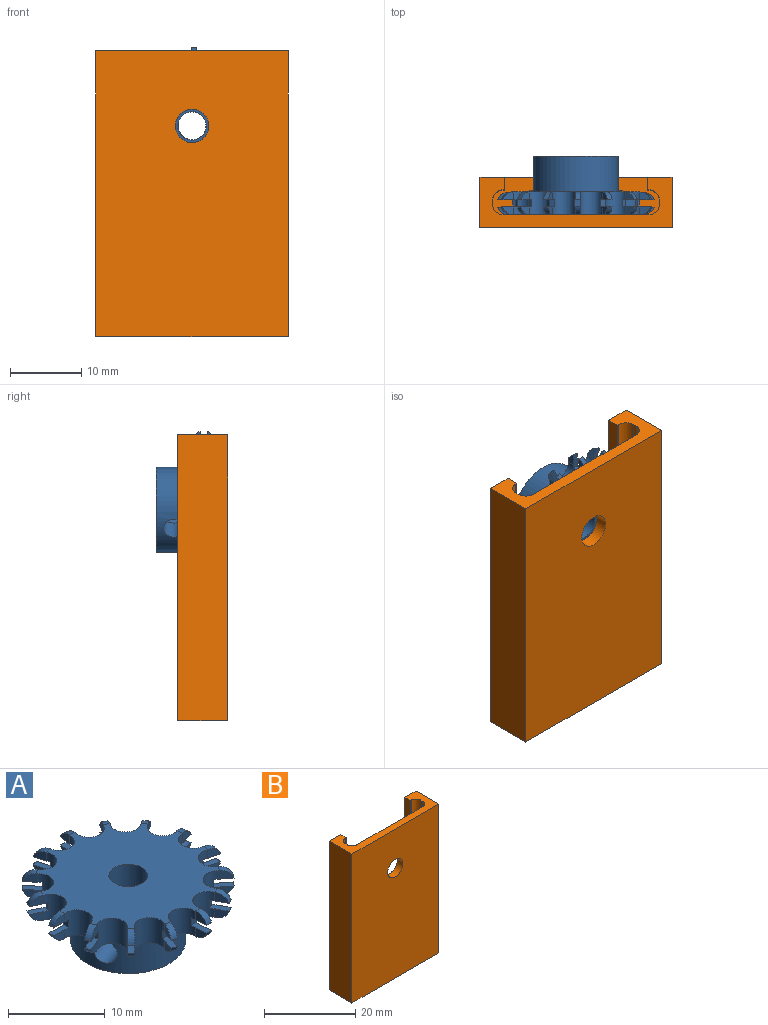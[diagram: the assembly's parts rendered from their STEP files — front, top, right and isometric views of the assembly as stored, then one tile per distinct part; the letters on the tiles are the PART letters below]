
ASSEMBLY  parts=2 mates=1
PART A: 186 faces, bbox 21.9x21.9x8.2 mm
  f0: plane 0.69x0.21mm, normal (-0.29,0.96,0), area 0mm2, adj f153,f183
  f1: plane 0.55x0.47mm, normal (-0.65,0.76,0), area 0mm2, adj f149,f181
  f2: plane 0.66x0.31mm, normal (-0.9,0.43,0), area 0mm2, adj f146,f179
  f3: plane 0.62x0.02mm, normal (-1,0.02,0), area 0mm2, adj f143,f177
  f4: plane 0.67x0.28mm, normal (-0.92,-0.39,0), area 0mm2, adj f140,f175
  f5: plane 0.53x0.5mm, normal (-0.69,-0.73,0), area 0mm2, adj f137,f173
  f6: plane 0.68x0.24mm, normal (-0.33,-0.94,0), area 0mm2, adj f134,f171
  f7: plane 0.72x0.06mm, normal (0.08,-1,0), area 0mm2, adj f131,f169
  f8: plane 0.64x0.35mm, normal (0.48,-0.88,0), area 0mm2, adj f128,f167
  f9: plane 0.58x0.44mm, normal (0.8,-0.61,0), area 0mm2, adj f125,f165
  f10: plane 0.71x0.17mm, normal (0.97,-0.23,0), area 0mm2, adj f122,f163
  f11: plane 0.71x0.13mm, normal (0.98,0.19,0), area 0mm2, adj f119,f161
  f12: plane 0.6x0.41mm, normal (0.82,0.57,0), area 0mm2, adj f116,f159
  f13: plane 0.62x0.38mm, normal (0.52,0.85,0), area 0mm2, adj f113,f157
  f14: plane 1.54x1.1mm, normal (0.96,0.29,0), area 1.3mm2, adj f84,f90,f154,f184
  f15: plane 1.57x1.13mm, normal (-0.96,-0.29,0), area 1.3mm2, adj f84,f91,f154,f184
  f16: plane 1.22x1.1mm, normal (0.76,0.65,0), area 1.3mm2, adj f84,f91,f150,f182
  f17: plane 1.25x1.13mm, normal (-0.76,-0.65,0), area 1.3mm2, adj f84,f92,f150,f182
  f18: plane 1.45x1.1mm, normal (0.43,0.9,0), area 1.3mm2, adj f84,f92,f147,f180
  f19: plane 1.48x1.13mm, normal (-0.43,-0.9,0), area 1.3mm2, adj f84,f93,f147,f180
  f20: plane 1.6x1.1mm, normal (0.02,1,0), area 1.3mm2, adj f84,f93,f144,f178
  f21: plane 1.63x1.13mm, normal (-0.02,-1,0), area 1.3mm2, adj f84,f94,f144,f178
  f22: plane 1.48x1.1mm, normal (-0.39,0.92,0), area 1.3mm2, adj f84,f94,f141,f176
  f23: plane 1.51x1.13mm, normal (0.39,-0.92,0), area 1.3mm2, adj f84,f95,f141,f176
  f24: plane 1.17x1.1mm, normal (-0.73,0.69,0), area 1.3mm2, adj f84,f95,f138,f174
  f25: plane 1.2x1.13mm, normal (0.73,-0.69,0), area 1.3mm2, adj f84,f96,f138,f174
  f26: plane 1.51x1.1mm, normal (-0.94,0.33,0), area 1.3mm2, adj f84,f96,f135,f172
  f27: plane 1.54x1.13mm, normal (0.94,-0.33,0), area 1.3mm2, adj f84,f97,f135,f172
  f28: plane 1.6x1.1mm, normal (-1,-0.08,0), area 1.3mm2, adj f84,f97,f132,f170
  f29: plane 1.63x1.13mm, normal (1,0.08,0), area 1.3mm2, adj f84,f98,f132,f170
  f30: plane 1.41x1.1mm, normal (-0.88,-0.48,0), area 1.3mm2, adj f84,f98,f129,f168
  f31: plane 1.44x1.13mm, normal (0.88,0.48,0), area 1.3mm2, adj f84,f99,f129,f168
  f32: plane 1.28x1.1mm, normal (-0.61,-0.8,0), area 1.3mm2, adj f84,f99,f126,f166
  f33: plane 1.31x1.13mm, normal (0.61,0.8,0), area 1.3mm2, adj f84,f100,f126,f166
  f34: plane 1.56x1.1mm, normal (-0.23,-0.97,0), area 1.3mm2, adj f84,f100,f123,f164
  f35: plane 1.59x1.13mm, normal (0.23,0.97,0), area 1.3mm2, adj f84,f101,f123,f164
  f36: plane 1.58x1.1mm, normal (0.19,-0.98,0), area 1.3mm2, adj f84,f101,f120,f162
  f37: plane 1.61x1.13mm, normal (-0.19,0.98,0), area 1.3mm2, adj f84,f102,f120,f162
  f38: plane 1.32x1.1mm, normal (0.57,-0.82,0), area 1.3mm2, adj f84,f102,f117,f160
  f39: plane 1.35x1.13mm, normal (-0.57,0.82,0), area 1.3mm2, adj f84,f103,f117,f160
  f40: plane 1.37x1.1mm, normal (0.85,-0.52,0), area 1.3mm2, adj f84,f103,f114,f158
  f41: plane 1.4x1.13mm, normal (-0.85,0.52,0), area 1.3mm2, adj f84,f104,f114,f158
  f42: plane 1.54x1.1mm, normal (0.96,0.29,0), area 1.3mm2, adj f85,f90,f153,f183
  f43: plane 0.69x0.21mm, normal (-0.29,0.96,0), area 0mm2, adj f154,f184
  f44: plane 1.57x1.13mm, normal (-0.96,-0.29,0), area 1.3mm2, adj f85,f91,f153,f183
  f45: plane 1.22x1.1mm, normal (0.76,0.65,0), area 1.3mm2, adj f85,f91,f149,f181
  f46: plane 0.55x0.47mm, normal (-0.65,0.76,0), area 0mm2, adj f150,f182
  f47: plane 1.25x1.13mm, normal (-0.76,-0.65,0), area 1.3mm2, adj f85,f92,f149,f181
  f48: plane 1.45x1.1mm, normal (0.43,0.9,0), area 1.3mm2, adj f85,f92,f146,f179
  f49: plane 0.66x0.31mm, normal (-0.9,0.43,0), area 0mm2, adj f147,f180
  f50: plane 1.48x1.13mm, normal (-0.43,-0.9,0), area 1.3mm2, adj f85,f93,f146,f179
  f51: plane 1.6x1.1mm, normal (0.02,1,0), area 1.3mm2, adj f85,f93,f143,f177
  f52: plane 0.62x0.02mm, normal (-1,0.02,0), area 0mm2, adj f144,f178
  f53: plane 1.63x1.13mm, normal (-0.02,-1,0), area 1.3mm2, adj f85,f94,f143,f177
  f54: plane 1.48x1.1mm, normal (-0.39,0.92,0), area 1.3mm2, adj f85,f94,f140,f175
  f55: plane 0.67x0.28mm, normal (-0.92,-0.39,0), area 0mm2, adj f141,f176
  f56: plane 1.51x1.13mm, normal (0.39,-0.92,0), area 1.3mm2, adj f85,f95,f140,f175
  f57: plane 1.17x1.1mm, normal (-0.73,0.69,0), area 1.3mm2, adj f85,f95,f137,f173
  f58: plane 0.53x0.5mm, normal (-0.69,-0.73,0), area 0mm2, adj f138,f174
  f59: plane 1.2x1.13mm, normal (0.73,-0.69,0), area 1.3mm2, adj f85,f96,f137,f173
  f60: plane 1.51x1.1mm, normal (-0.94,0.33,0), area 1.3mm2, adj f85,f96,f134,f171
  f61: plane 0.68x0.24mm, normal (-0.33,-0.94,0), area 0mm2, adj f135,f172
  f62: plane 1.54x1.13mm, normal (0.94,-0.33,0), area 1.3mm2, adj f85,f97,f134,f171
  f63: plane 1.6x1.1mm, normal (-1,-0.08,0), area 1.3mm2, adj f85,f97,f131,f169
  f64: plane 0.72x0.06mm, normal (0.08,-1,0), area 0mm2, adj f132,f170
  f65: plane 1.63x1.13mm, normal (1,0.08,0), area 1.3mm2, adj f85,f98,f131,f169
  f66: plane 1.41x1.1mm, normal (-0.88,-0.48,0), area 1.3mm2, adj f85,f98,f128,f167
  f67: plane 0.64x0.35mm, normal (0.48,-0.88,0), area 0mm2, adj f129,f168
  f68: plane 1.44x1.13mm, normal (0.88,0.48,0), area 1.3mm2, adj f85,f99,f128,f167
  f69: plane 1.28x1.1mm, normal (-0.61,-0.8,0), area 1.3mm2, adj f85,f99,f125,f165
  f70: plane 0.58x0.44mm, normal (0.8,-0.61,0), area 0mm2, adj f126,f166
  f71: plane 1.31x1.13mm, normal (0.61,0.8,0), area 1.3mm2, adj f85,f100,f125,f165
  f72: plane 1.56x1.1mm, normal (-0.23,-0.97,0), area 1.3mm2, adj f85,f100,f122,f163
  f73: plane 0.71x0.17mm, normal (0.97,-0.23,0), area 0mm2, adj f123,f164
  f74: plane 1.59x1.13mm, normal (0.23,0.97,0), area 1.3mm2, adj f85,f101,f122,f163
  f75: plane 1.58x1.1mm, normal (0.19,-0.98,0), area 1.3mm2, adj f85,f101,f119,f161
  f76: plane 0.71x0.13mm, normal (0.98,0.19,0), area 0mm2, adj f120,f162
  f77: plane 1.61x1.13mm, normal (-0.19,0.98,0), area 1.3mm2, adj f85,f102,f119,f161
  f78: plane 1.32x1.1mm, normal (0.57,-0.82,0), area 1.3mm2, adj f85,f102,f116,f159
  f79: plane 0.6x0.41mm, normal (0.82,0.57,0), area 0mm2, adj f117,f160
  f80: plane 1.35x1.13mm, normal (-0.57,0.82,0), area 1.3mm2, adj f85,f103,f116,f159
  f81: plane 1.37x1.1mm, normal (0.85,-0.52,0), area 1.3mm2, adj f85,f103,f113,f157
  f82: plane 0.62x0.38mm, normal (0.52,0.85,0), area 0mm2, adj f114,f158
  f83: plane 1.4x1.13mm, normal (-0.85,0.52,0), area 1.3mm2, adj f85,f104,f113,f157
  f84: plane 18.88x18.82mm, normal (0,0,1), area 206.5mm2, adj f14,f15,f16,f17,f18,f19,f20,f21
  f85: plane 18.88x18.82mm, normal (0,0,-1), area 107.9mm2, adj f42,f44,f45,f47,f48,f50,f51,f53
  f86: plane 1.59x1.1mm, normal (0.99,-0.13,0), area 1.3mm2, adj f84,f104,f110,f156
  f87: plane 1.59x1.1mm, normal (-0.99,0.13,0), area 1.3mm2, adj f84,f90,f110,f156
  f88: plane 1.59x1.1mm, normal (0.99,-0.13,0), area 1.3mm2, adj f85,f104,f111,f155
  f89: plane 1.59x1.1mm, normal (-0.99,0.13,0), area 1.3mm2, adj f85,f90,f111,f155
  f90: cylinder r=1.6mm len=3.2mm, axis (0,0,-1), area 14.2mm2, adj f14,f42,f84,f85,f87,f89,f110,f111
  f91: cylinder r=1.6mm len=3.2mm, axis (0,0,-1), area 14.2mm2, adj f15,f16,f44,f45,f84,f85,f149,f150
  f92: cylinder r=1.6mm len=3.2mm, axis (0,0,-1), area 14.2mm2, adj f17,f18,f47,f48,f84,f85,f146,f147
  f93: cylinder r=1.6mm len=3.2mm, axis (0,0,-1), area 14.2mm2, adj f19,f20,f50,f51,f84,f85,f143,f144
  f94: cylinder r=1.6mm len=3.2mm, axis (0,0,-1), area 14.2mm2, adj f21,f22,f53,f54,f84,f85,f140,f141
  f95: cylinder r=1.6mm len=3.2mm, axis (0,0,-1), area 14.2mm2, adj f23,f24,f56,f57,f84,f85,f137,f138
  f96: cylinder r=1.6mm len=3.2mm, axis (0,0,-1), area 14.2mm2, adj f25,f26,f59,f60,f84,f85,f134,f135
  f97: cylinder r=1.6mm len=3.2mm, axis (0,0,-1), area 14.2mm2, adj f27,f28,f62,f63,f84,f85,f131,f132
  f98: cylinder r=1.6mm len=3.2mm, axis (0,0,-1), area 14.2mm2, adj f29,f30,f65,f66,f84,f85,f128,f129
  f99: cylinder r=1.6mm len=3.2mm, axis (0,0,-1), area 14.2mm2, adj f31,f32,f68,f69,f84,f85,f125,f126
  f100: cylinder r=1.6mm len=3.2mm, axis (0,0,-1), area 14.2mm2, adj f33,f34,f71,f72,f84,f85,f122,f123
  f101: cylinder r=1.6mm len=3.2mm, axis (0,0,-1), area 14.2mm2, adj f35,f36,f74,f75,f84,f85,f119,f120
  f102: cylinder r=1.6mm len=3.2mm, axis (0,0,-1), area 14.2mm2, adj f37,f38,f77,f78,f84,f85,f116,f117
  f103: cylinder r=1.6mm len=3.2mm, axis (0,0,-1), area 14.2mm2, adj f39,f40,f80,f81,f84,f85,f113,f114
  f104: cylinder r=1.6mm len=3.2mm, axis (0,0,-1), area 14.2mm2, adj f41,f83,f84,f85,f86,f88,f110,f111
  f105: cylinder r=1.95mm len=5mm, axis (0,0,1), area 54.6mm2, adj f107,f108,f185
  f106: cylinder r=5.95mm len=11.9mm, axis (0,0,1), area 180.7mm2, adj f85,f107,f185
  f107: plane 11.9x11.9mm, normal (0,0,-1), area 99.3mm2, adj f105,f106
  f108: plane 4x4mm, normal (0,0,1), area 0.6mm2, adj f105,f109
  f109: cylinder r=2mm len=4mm, axis (0,0,-1), area 40.2mm2, adj f84,f108
  f110: plane 2.18x1mm, normal (0,0,-1), area 1.5mm2, adj f86,f87,f90,f104,f112,f156
  f111: plane 2.18x1mm, normal (0,0,1), area 1.5mm2, adj f88,f89,f90,f104,f112,f155
  f112: cylinder r=8.88mm len=1mm, axis (0,0,1), area 0.8mm2, adj f90,f104,f110,f111
  f113: plane 2.18x1.73mm, normal (0,0,1), area 1.5mm2, adj f13,f81,f83,f103,f104,f115
  f114: plane 2.18x1.73mm, normal (0,0,-1), area 1.5mm2, adj f40,f41,f82,f103,f104,f115
  f115: cylinder r=8.88mm len=1mm, axis (0,0,1), area 0.8mm2, adj f103,f104,f113,f114
  f116: plane 2.15x1.81mm, normal (0,0,1), area 1.5mm2, adj f12,f78,f80,f102,f103,f118
  f117: plane 2.15x1.81mm, normal (0,0,-1), area 1.5mm2, adj f38,f39,f79,f102,f103,f118
  f118: cylinder r=8.88mm len=1mm, axis (0,0,1), area 0.8mm2, adj f102,f103,f116,f117
  f119: plane 2.2x1.12mm, normal (0,0,1), area 1.5mm2, adj f11,f75,f77,f101,f102,f121
  f120: plane 2.2x1.12mm, normal (0,0,-1), area 1.5mm2, adj f36,f37,f76,f101,f102,f121
  f121: cylinder r=8.88mm len=1mm, axis (0,0,1), area 0.8mm2, adj f101,f102,f119,f120
  f122: plane 2.22x1.21mm, normal (0,0,1), area 1.5mm2, adj f10,f72,f74,f100,f101,f124
  f123: plane 2.22x1.21mm, normal (0,0,-1), area 1.5mm2, adj f34,f35,f73,f100,f101,f124
  f124: cylinder r=8.88mm len=1mm, axis (0,0,1), area 0.8mm2, adj f100,f101,f122,f123
  f125: plane 2.12x1.86mm, normal (0,0,1), area 1.5mm2, adj f9,f69,f71,f99,f100,f127
  f126: plane 2.12x1.86mm, normal (0,0,-1), area 1.5mm2, adj f32,f33,f70,f99,f100,f127
  f127: cylinder r=8.88mm len=1mm, axis (0,0,1), area 0.8mm2, adj f99,f100,f125,f126
  f128: plane 2.2x1.66mm, normal (0,0,1), area 1.5mm2, adj f8,f66,f68,f98,f99,f130
  f129: plane 2.2x1.66mm, normal (0,0,-1), area 1.5mm2, adj f30,f31,f67,f98,f99,f130
  f130: cylinder r=8.88mm len=1mm, axis (0,0,1), area 0.8mm2, adj f98,f99,f128,f129
  f131: plane 2.16x0.91mm, normal (0,0,1), area 1.5mm2, adj f7,f63,f65,f97,f98,f133
  f132: plane 2.16x0.91mm, normal (0,0,-1), area 1.5mm2, adj f28,f29,f64,f97,f98,f133
  f133: cylinder r=8.88mm len=1mm, axis (0,0,1), area 0.8mm2, adj f97,f98,f131,f132
  f134: plane 2.23x1.4mm, normal (0,0,1), area 1.5mm2, adj f6,f60,f62,f96,f97,f136
  f135: plane 2.23x1.4mm, normal (0,0,-1), area 1.5mm2, adj f26,f27,f61,f96,f97,f136
  f136: cylinder r=8.88mm len=1mm, axis (0,0,1), area 0.8mm2, adj f96,f97,f134,f135
  f137: plane 2.04x1.98mm, normal (0,0,1), area 1.5mm2, adj f5,f57,f59,f95,f96,f139
  f138: plane 2.04x1.98mm, normal (0,0,-1), area 1.5mm2, adj f24,f25,f58,f95,f96,f139
  f139: cylinder r=8.88mm len=1mm, axis (0,0,1), area 0.8mm2, adj f95,f96,f137,f138
  f140: plane 2.23x1.49mm, normal (0,0,1), area 1.5mm2, adj f4,f54,f56,f94,f95,f142
  f141: plane 2.23x1.49mm, normal (0,0,-1), area 1.5mm2, adj f22,f23,f55,f94,f95,f142
  f142: cylinder r=8.88mm len=1mm, axis (0,0,1), area 0.8mm2, adj f94,f95,f140,f141
  f143: plane 2.12x0.8mm, normal (0,0,1), area 1.5mm2, adj f3,f51,f53,f93,f94,f145,f177
  f144: plane 2.12x0.8mm, normal (0,0,-1), area 1.5mm2, adj f20,f21,f52,f93,f94,f145,f178
  f145: cylinder r=8.88mm len=1mm, axis (0,0,1), area 0.8mm2, adj f93,f94,f143,f144
  f146: plane 2.22x1.57mm, normal (0,0,1), area 1.5mm2, adj f2,f48,f50,f92,f93,f148
  f147: plane 2.22x1.57mm, normal (0,0,-1), area 1.5mm2, adj f18,f19,f49,f92,f93,f148
  f148: cylinder r=8.88mm len=1mm, axis (0,0,1), area 0.8mm2, adj f92,f93,f146,f147
  f149: plane 2.08x1.93mm, normal (0,0,1), area 1.5mm2, adj f1,f45,f47,f91,f92,f151
  f150: plane 2.08x1.93mm, normal (0,0,-1), area 1.5mm2, adj f16,f17,f46,f91,f92,f151
  f151: cylinder r=8.88mm len=1mm, axis (0,0,1), area 0.8mm2, adj f91,f92,f149,f150
  f152: cylinder r=8.88mm len=1mm, axis (0,0,1), area 0.8mm2, adj f90,f91,f153,f154
  f153: plane 2.23x1.31mm, normal (0,0,1), area 1.5mm2, adj f0,f42,f44,f90,f91,f152
  f154: plane 2.23x1.31mm, normal (0,0,-1), area 1.5mm2, adj f14,f15,f43,f90,f91,f152
  f155: cylinder r=1.6mm len=1.6mm, axis (-0.99,0.13,0), area 1.5mm2, adj f85,f88,f89,f111
  f156: cylinder r=1.6mm len=1.6mm, axis (-0.99,0.13,0), area 1.5mm2, adj f84,f86,f87,f110
  f157: revolved ~1.73x1.41mm, area 1.5mm2, adj f13,f81,f83,f85
  f158: revolved ~1.73x1.41mm, area 1.5mm2, adj f40,f41,f82,f84
  f159: revolved ~1.66x1.55mm, area 1.5mm2, adj f12,f78,f80,f85
  f160: revolved ~1.66x1.55mm, area 1.5mm2, adj f38,f39,f79,f84
  f161: revolved ~1.63x1.11mm, area 1.5mm2, adj f11,f75,f77,f85
  f162: revolved ~1.63x1.11mm, area 1.5mm2, adj f36,f37,f76,f84
  f163: revolved ~1.67x1.1mm, area 1.5mm2, adj f10,f72,f74,f85
  f164: revolved ~1.67x1.1mm, area 1.5mm2, adj f34,f35,f73,f84
  f165: revolved ~1.71x1.5mm, area 1.5mm2, adj f9,f69,f71,f85
  f166: revolved ~1.71x1.5mm, area 1.5mm2, adj f32,f33,f70,f84
  f167: revolved ~1.68x1.46mm, area 1.5mm2, adj f8,f66,f68,f85
  f168: revolved ~1.68x1.46mm, area 1.5mm2, adj f30,f31,f67,f84
  f169: revolved ~1.57x1.1mm, area 1.5mm2, adj f7,f63,f65,f85
  f170: revolved ~1.57x1.1mm, area 1.5mm2, adj f28,f29,f64,f84
  f171: revolved ~1.71x1.19mm, area 1.5mm2, adj f6,f60,f62,f85
  f172: revolved ~1.71x1.19mm, area 1.5mm2, adj f26,f27,f61,f84
  f173: revolved ~1.68x1.57mm, area 1.5mm2, adj f5,f57,f59,f85
  f174: revolved ~1.68x1.57mm, area 1.5mm2, adj f24,f25,f58,f84
  f175: revolved ~1.68x1.36mm, area 1.5mm2, adj f4,f54,f56,f85
  f176: revolved ~1.68x1.36mm, area 1.5mm2, adj f22,f23,f55,f84
  f177: revolved ~1.54x1.1mm, area 1.5mm2, adj f3,f51,f53,f85,f143
  f178: revolved ~1.54x1.1mm, area 1.5mm2, adj f20,f21,f52,f84,f144
  f179: revolved ~1.73x1.31mm, area 1.5mm2, adj f2,f48,f50,f85
  f180: revolved ~1.73x1.31mm, area 1.5mm2, adj f18,f19,f49,f84
  f181: revolved ~1.63x1.63mm, area 1.5mm2, adj f1,f45,f47,f85
  f182: revolved ~1.63x1.63mm, area 1.5mm2, adj f16,f17,f46,f84
  f183: revolved ~1.66x1.24mm, area 1.5mm2, adj f0,f42,f44,f85
  f184: revolved ~1.66x1.24mm, area 1.5mm2, adj f14,f15,f43,f84
  f185: cylinder r=1.4mm len=5.13mm, axis (0.94,0.35,0), area 38.9mm2, adj f105,f106
PART B: 43 faces, bbox 27.5x7.6x40.6 mm
  f0: plane 7.58x5.38mm, normal (0,0,1), area 22.1mm2, adj f1,f2,f5,f6,f7,f11,f19,f23
  f1: plane 7.23x1.38mm, normal (-0.98,0,-0.19), area 5.9mm2, adj f0,f3,f32,f34,f36
  f2: plane 30.24x20.64mm, normal (0,1,0), area 485mm2, adj f0,f3,f4,f15,f16,f17,f22,f23
  f3: plane 1.88x1.88mm, normal (0,0,1), area 0.1mm2, adj f1,f2,f19,f34
  f4: plane 8.08x5.88mm, normal (0,0,1), area 22.1mm2, adj f2,f11,f12,f13,f14,f20,f21,f22
  f5: plane 30x0.5mm, normal (1,0,0), area 15mm2, adj f0,f15,f23,f24
  f6: plane 30x0.25mm, normal (0,-1,0), area 7.5mm2, adj f0,f7,f15,f24
  f7: plane 30x1.75mm, normal (1,0,0), area 52.5mm2, adj f0,f6,f11,f15
  f8: plane 40x7mm, normal (-1,0,0), area 280mm2, adj f9,f11,f15,f18
  f9: plane 40x26.9mm, normal (0,-1,0), area 1058.7mm2, adj f8,f10,f15,f16,f18
  f10: plane 40x7mm, normal (1,0,0), area 280mm2, adj f9,f11,f15,f18
  f11: plane 40x26.9mm, normal (0,1,0), area 576mm2, adj f0,f4,f7,f8,f10,f12,f15,f18
  f12: plane 30x1.75mm, normal (-1,0,0), area 52.5mm2, adj f4,f11,f13,f15
  f13: plane 30x0.25mm, normal (0,-1,0), area 7.5mm2, adj f4,f12,f15,f21
  f14: plane 30x0.5mm, normal (-1,0,0), area 15mm2, adj f4,f15,f21,f22
  f15: plane 26.9x7mm, normal (0,0,1), area 73.5mm2, adj f2,f5,f6,f7,f8,f9,f10,f11
  f16: cylinder r=2.35mm len=4.7mm, axis (0,1,0), area 25.8mm2, adj f2,f9
  f17: plane 2.25x2.25mm, normal (0,0,1), area 0.1mm2, adj f2,f20,f26,f33
  f18: plane 26.9x7mm, normal (0,0,-1), area 140.5mm2, adj f8,f9,f10,f11,f41,f42
  f19: bspline ~10x7mm, area 100.1mm2, adj f0,f3,f42
  f20: bspline ~8.81x5.25mm, area 97.8mm2, adj f4,f17,f41
  f21: cylinder r=1.5mm len=30mm, axis (0,0,1), area 70.7mm2, adj f4,f13,f14,f15
  f22: cylinder r=1.5mm len=30mm, axis (0,0,-1), area 70.7mm2, adj f2,f4,f14,f15
  f23: cylinder r=1.5mm len=30mm, axis (0,0,1), area 70.7mm2, adj f0,f2,f5,f15
  f24: cylinder r=1.5mm len=30mm, axis (0,0,1), area 70.7mm2, adj f0,f5,f6,f15
  f25: cylinder r=11.94mm len=12mm, axis (0,-1,0), area 51.1mm2, adj f2,f11,f28,f30,f35,f36,f37,f38
  f26: plane 7.23x1.38mm, normal (0.98,0,-0.19), area 5.9mm2, adj f4,f17,f31,f33,f39
  f27: plane 0.64x0.12mm, normal (0,-1,0), area 0mm2, adj f0,f28,f32
  f28: plane 9.46x2.2mm, normal (-1,0,0), area 13.3mm2, adj f0,f11,f25,f27,f32,f37
  f29: plane 0.64x0.12mm, normal (0,-1,0), area 0mm2, adj f4,f30,f31
  f30: plane 9.45x2.2mm, normal (1,0,0), area 13.3mm2, adj f4,f11,f25,f29,f31,f40
  f31: cylinder r=1.6mm len=7.86mm, axis (0.19,0,0.98), area 14.2mm2, adj f4,f26,f29,f30,f40
  f32: cylinder r=1.6mm len=7.86mm, axis (0.19,0,-0.98), area 14.2mm2, adj f0,f1,f27,f28,f37
  f33: cylinder r=1.6mm len=9.62mm, axis (-0.19,0,-0.98), area 20.8mm2, adj f2,f17,f26,f38
  f34: cylinder r=1.6mm len=9.62mm, axis (-0.19,0,0.98), area 20.8mm2, adj f1,f2,f3,f35
  f35: bspline ~3.59x3.11mm, area 4.6mm2, adj f2,f25,f34,f36
  f36: cylinder r=1mm len=1.36mm, axis (0,-1,0), area 1.7mm2, adj f1,f25,f35,f37
  f37: bspline ~3.08x2.98mm, area 3.8mm2, adj f25,f28,f32,f36
  f38: bspline ~3.59x3.11mm, area 4.6mm2, adj f2,f25,f33,f39
  f39: cylinder r=1mm len=1.36mm, axis (0,-1,0), area 1.7mm2, adj f25,f26,f38,f40
  f40: bspline ~3.08x2.98mm, area 3.8mm2, adj f25,f30,f31,f39
  f41: bspline ~5.54x5.51mm, area 21mm2, adj f18,f20
  f42: bspline ~5.54x5.51mm, area 21mm2, adj f18,f19
PLACE A rot(axis=(1,-0.05,0.05),90.1deg) t=(-3.35,-6.77,8.35)mm
PLACE B rot(axis=(-0.37,-0.05,0.93),0deg) t=(-7.24,0.75,-11.15)mm fixed
MATE revolute A.f112 <-> B.f16  axis (0,-1,0) through (-3.35,-9.97,8.35)mm
